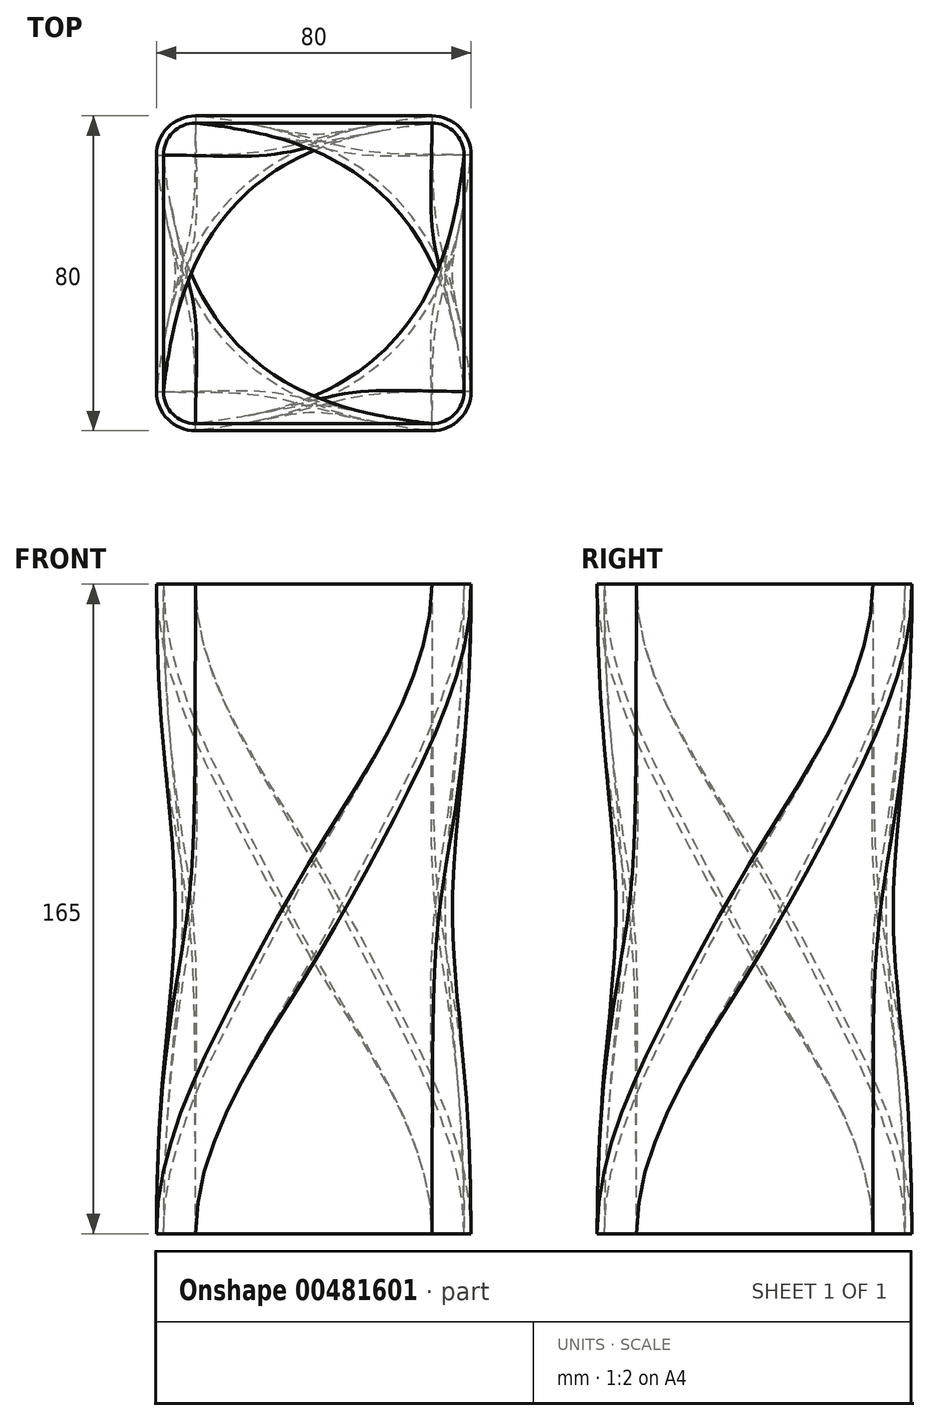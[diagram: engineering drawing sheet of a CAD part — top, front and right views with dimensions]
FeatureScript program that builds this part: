
annotation { "Feature Type Name" : "Feature", "Feature Type Description" : "" }
export const myFeature = defineFeature(function(context is Context, id is Id, definition is map)
    precondition{}
    {
        {
            var Q0;
            Q0=qCreatedBy(makeId("Top.planeOp"),FACE);
            var sketch = newSketch(context, id + "F0", { "sketchPlane" : qUnion([Q0])});
            skLineSegment(sketch, "E0.bottom", {"start": v(40, -40) * mm, "end": v(-40, -40) * mm});
            skLineSegment(sketch, "E0.top", {"start": v(40, 40) * mm, "end": v(-40, 40) * mm});
            skLineSegment(sketch, "E0.left", {"start": v(40, -40) * mm, "end": v(40, 40) * mm});
            skLineSegment(sketch, "E0.right", {"start": v(-40, -40) * mm, "end": v(-40, 40) * mm});
            skPoint(sketch, "E0.middle", {"position": v(0, 0) * mm});
            skSolve(sketch);
        }
        {
            var Q0;
            Q0=makeQuery(id+"F0.imprint","IMPRINT",FACE,{"disambiguationData":[TD([[makeQuery(id+"F0.imprint","IMPRINT",EDGE,{"derivedFrom":sQuery(id+"F0.wireOp",EDGE,"E0.bottom")}),-1.0]])]});
            cPlane(context, id + "F1", {"entities" : qUnion([Q0]), "cplaneType" : CPlaneType.OFFSET, "offset" : 165 * mm, "width" : 150 * mm, "height" : 150 * mm});
        }
        {
            var Q0;
            Q0=qCreatedBy(id+"F1.planeOp",FACE);
            var sketch = newSketch(context, id + "F2", { "sketchPlane" : qUnion([Q0])});
            skLineSegment(sketch, "E1.bottom", {"start": v(40, -40) * mm, "end": v(-40, -40) * mm});
            skLineSegment(sketch, "E1.top", {"start": v(40, 40) * mm, "end": v(-40, 40) * mm});
            skLineSegment(sketch, "E1.left", {"start": v(40, -40) * mm, "end": v(40, 40) * mm});
            skLineSegment(sketch, "E1.right", {"start": v(-40, -40) * mm, "end": v(-40, 40) * mm});
            skPoint(sketch, "E1.middle", {"position": v(0, 0) * mm});
            skSolve(sketch);
        }
        {
            var Q0;
            Q0=makeQuery(id+"F0.imprint","IMPRINT",FACE,{"disambiguationData":[TD([[makeQuery(id+"F0.imprint","IMPRINT",EDGE,{"derivedFrom":sQuery(id+"F0.wireOp",EDGE,"E0.bottom")}),-1.0]])]});
            var Q1;
            Q1=makeQuery(id+"F2.imprint","IMPRINT",FACE,{"disambiguationData":[TD([[makeQuery(id+"F2.imprint","IMPRINT",EDGE,{"derivedFrom":sQuery(id+"F2.wireOp",EDGE,"E1.bottom")}),-1.0]])]});
            var Q2;
            Q2=sQuery(id+"F0.wireOp",VERTEX,"E0.right.start");
            var Q3;
            Q3=sQuery(id+"F2.wireOp",VERTEX,"E1.left.start");
            loft(context, id + "F3", {"startCondition" : LoftEndDerivativeType.NORMAL_TO_PROFILE, "startMagnitude" : 1, "endCondition" : LoftEndDerivativeType.NORMAL_TO_PROFILE, "endMagnitude" : 1, "sheetProfilesArray" : [{ "sheetProfileEntities" : qUnion([Q0]) }, { "sheetProfileEntities" : qUnion([Q1]) }], "matchConnections" : true, "connections" : [{ "connectionEntities" : qUnion([Q2, Q3]), "connectionEdgeQueries" : qUnion([]), "connectionEdgeParameters" : [] }]});
        }
        {
            var Q0;
            Q0=makeQuery(id+"F3.opLoft","SWEPT_EDGE",EDGE,{"disambiguationData":[OSD([sQuery(id+"F0.wireOp",EDGE,"E0.top"),sQuery(id+"F0.wireOp",EDGE,"E0.left"),sQuery(id+"F2.wireOp",EDGE,"E1.top"),sQuery(id+"F2.wireOp",EDGE,"E1.right")])]});
            var Q1;
            Q1=makeQuery(id+"F3.opLoft","SWEPT_EDGE",EDGE,{"disambiguationData":[OSD([sQuery(id+"F0.wireOp",EDGE,"E0.top"),sQuery(id+"F0.wireOp",EDGE,"E0.right"),sQuery(id+"F2.wireOp",EDGE,"E1.bottom"),sQuery(id+"F2.wireOp",EDGE,"E1.right")])]});
            var Q2;
            Q2=makeQuery(id+"F3.opLoft","SWEPT_EDGE",EDGE,{"disambiguationData":[OSD([sQuery(id+"F0.wireOp",EDGE,"E0.bottom"),sQuery(id+"F0.wireOp",EDGE,"E0.right"),sQuery(id+"F2.wireOp",EDGE,"E1.bottom"),sQuery(id+"F2.wireOp",EDGE,"E1.left")])]});
            var Q3;
            Q3=makeQuery(id+"F3.opLoft","SWEPT_EDGE",EDGE,{"disambiguationData":[OSD([sQuery(id+"F0.wireOp",EDGE,"E0.bottom"),sQuery(id+"F0.wireOp",EDGE,"E0.left"),sQuery(id+"F2.wireOp",EDGE,"E1.top"),sQuery(id+"F2.wireOp",EDGE,"E1.left")])]});
            fillet(context, id + "F4", {"entities" : qUnion([Q0, Q1, Q2, Q3]), "radius" : 10 * mm, "tangentPropagation" : true, "allowEdgeOverflow" : false});
        }
        {
            var Q0;
            Q0=makeQuery(id+"F3.opLoft","CAP_FACE",FACE,{"disambiguationData":[OSD([makeQuery(id+"F2.imprint","IMPRINT",FACE,{"disambiguationData":[TD([[makeQuery(id+"F2.imprint","IMPRINT",EDGE,{"derivedFrom":sQuery(id+"F2.wireOp",EDGE,"E1.bottom")}),-1.0]])]})])],"isStart":true});
            var Q1;
            Q1=makeQuery(id+"F3.opLoft","CAP_FACE",FACE,{"disambiguationData":[OSD([makeQuery(id+"F0.imprint","IMPRINT",FACE,{"disambiguationData":[TD([[makeQuery(id+"F0.imprint","IMPRINT",EDGE,{"derivedFrom":sQuery(id+"F0.wireOp",EDGE,"E0.bottom")}),-1.0]])]})])],"isStart":true});
            shell(context, id + "F5", {"entities" : qUnion([Q0, Q1]), "thickness" : (0.45 * 4) * mm});
        }
        {
            var Q0;
            Q0=makeQuery(id+"F3.opLoft","CAP_FACE",FACE,{"disambiguationData":[OSD([makeQuery(id+"F2.imprint","IMPRINT",FACE,{"disambiguationData":[TD([[makeQuery(id+"F2.imprint","IMPRINT",EDGE,{"derivedFrom":sQuery(id+"F2.wireOp",EDGE,"E1.bottom")}),-1.0]])]})])],"isStart":true});
            cPlane(context, id + "F6", {"entities" : qUnion([Q0]), "cplaneType" : CPlaneType.OFFSET, "offset" : 0.9 * mm, "oppositeDirection" : true, "width" : 150 * mm, "height" : 150 * mm});
        }
    });
